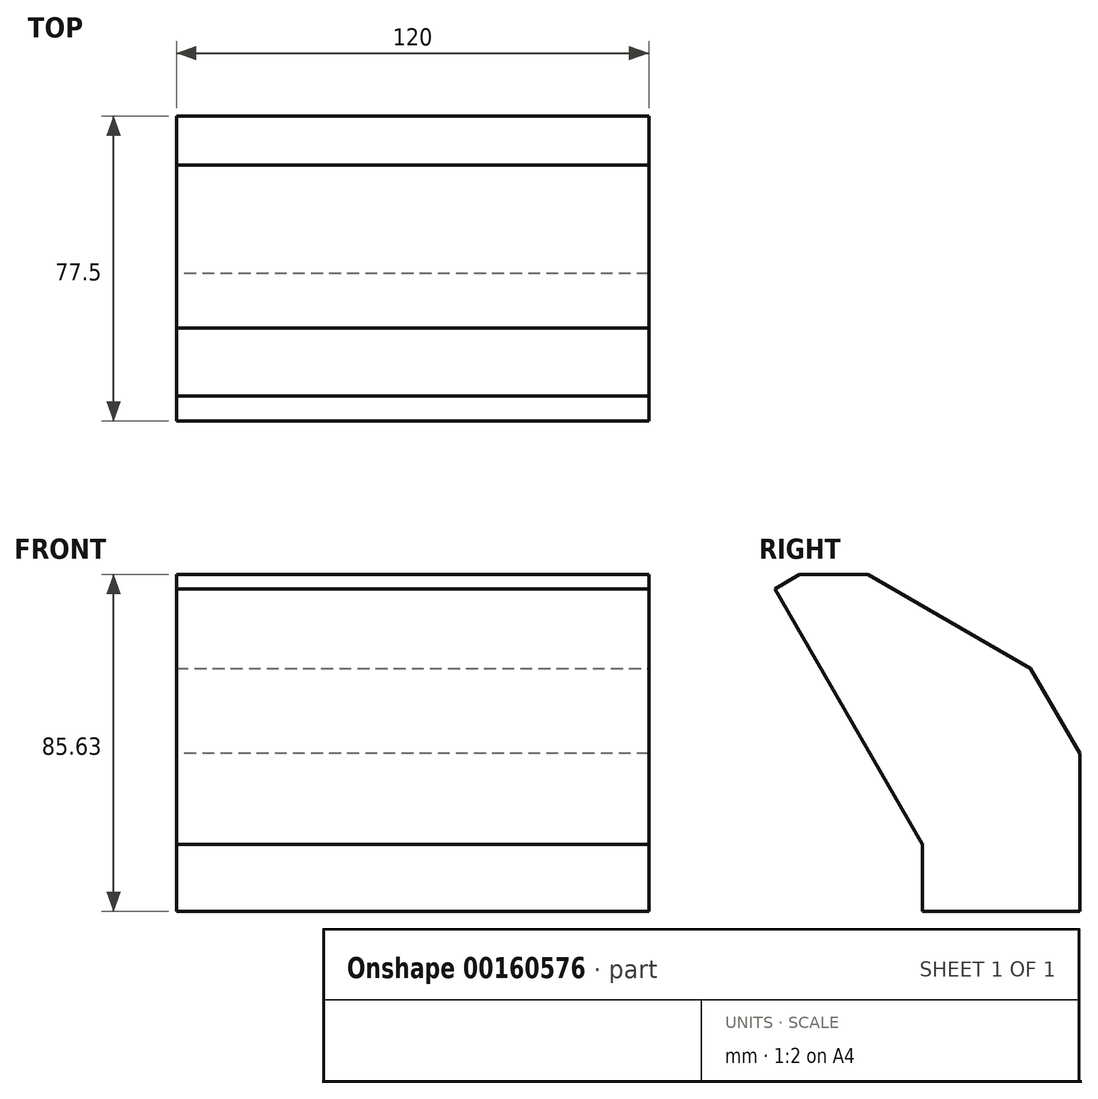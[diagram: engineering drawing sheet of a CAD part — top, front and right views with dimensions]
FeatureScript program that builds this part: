
annotation { "Feature Type Name" : "Feature", "Feature Type Description" : "" }
export const myFeature = defineFeature(function(context is Context, id is Id, definition is map)
    precondition{}
    {
        {
            var Q0;
            Q0=qCreatedBy(makeId("Top.planeOp"),FACE);
            var sketch = newSketch(context, id + "F0", { "sketchPlane" : qUnion([Q0])});
            skLineSegment(sketch, "E0.bottom", {"start": v(60, -20) * mm, "end": v(-60, -20) * mm});
            skLineSegment(sketch, "E0.top", {"start": v(60, 20) * mm, "end": v(-60, 20) * mm});
            skLineSegment(sketch, "E0.left", {"start": v(60, -20) * mm, "end": v(60, 20) * mm});
            skLineSegment(sketch, "E0.right", {"start": v(-60, -20) * mm, "end": v(-60, 20) * mm});
            skPoint(sketch, "E0.middle", {"position": v(0, 0) * mm});
            skLineSegment(sketch, "E1", {"start": v(-60, 0) * mm, "end": v(60, 0) * mm, "construction": true});
            skLineSegment(sketch, "E2", {"start": v(0, 0) * mm, "end": v(-45, 0) * mm, "construction": true});
            skLineSegment(sketch, "E3", {"start": v(0, 0) * mm, "end": v(45, 0) * mm, "construction": true});
            skCircle(sketch, "E4", {"center": v(-45, 0) * mm, "radius": 3 * mm});
            skCircle(sketch, "E5", {"center": v(45, 0) * mm, "radius": 3 * mm});
            skSolve(sketch);
        }
        {
            var Q0;
            Q0=makeQuery(id+"F0.imprint","IMPRINT",FACE,{"disambiguationData":[TD([[makeQuery(id+"F0.imprint","IMPRINT",EDGE,{"derivedFrom":sQuery(id+"F0.wireOp",EDGE,"E0.bottom")}),-1.0]])]});
            var Q1;
            Q1=makeQuery(id+"F0.imprint","IMPRINT",FACE,{"disambiguationData":[TD([[makeQuery(id+"F0.imprint","IMPRINT",EDGE,{"derivedFrom":sQuery(id+"F0.wireOp",EDGE,"E4")}),1.0]])]});
            var Q2;
            Q2=makeQuery(id+"F0.imprint","IMPRINT",FACE,{"disambiguationData":[TD([[makeQuery(id+"F0.imprint","IMPRINT",EDGE,{"derivedFrom":sQuery(id+"F0.wireOp",EDGE,"E5")}),1.0]])]});
            extrude(context, id + "F1", {"entities" : qUnion([Q0, Q1, Q2]), "depth" : 43 * mm});
        }
        {
            var Q0;
            Q0=makeQuery(id+"F1.opExtrude","CAP_EDGE",EDGE,{"disambiguationData":[OSD([sQuery(id+"F0.wireOp",EDGE,"E0.bottom")])],"isStart":false});
            chamfer(context, id + "F2", {"entities" : qUnion([Q0]), "chamferType" : ChamferType.OFFSET_ANGLE, "width" : 45 * mm, "oppositeDirection" : true, "angle" : 30 * degree, "tangentPropagation" : true});
        }
        {
            var Q0;
            Q0=makeQuery(id+"F2.opChamfer","BLEND_FACE",FACE,{"disambiguationData":[OSD([sQuery(id+"F0.wireOp",EDGE,"E0.bottom")])]});
            extrude(context, id + "F3", {"entities" : qUnion([Q0]), "operationType" : NewBodyOperationType.ADD, "depth" : 75 * mm});
        }
        {
            var Q0;
            Q0=makeQuery(id+"F3.opExtrude","CAP_EDGE",EDGE,{"disambiguationData":[OSD([sQuery(id+"F0.wireOp",EDGE,"E0.bottom"),sQuery(id+"F0.wireOp",EDGE,"E0.top")])],"isStart":false});
            chamfer(context, id + "F4", {"entities" : qUnion([Q0]), "chamferType" : ChamferType.OFFSET_ANGLE, "width" : 50 * mm, "oppositeDirection" : false, "angle" : 30 * degree, "tangentPropagation" : true});
        }
        {
            var Q0;
            {var subQ0=sQuery(id+"F0.wireOp",EDGE,"E0.bottom");Q0=makeQuery(id+"F4.opChamfer","BLEND_EDGE",EDGE,{"blendedFrom":[makeQuery(id+"F3.opExtrude","CAP_EDGE",EDGE,{"disambiguationData":[OSD([subQ0,sQuery(id+"F0.wireOp",EDGE,"E0.top")])],"isStart":false}),makeQuery(id+"F3.opExtrude","CAP_FACE",FACE,{"disambiguationData":[OSD([subQ0])],"isStart":false})],"blendedInto":[makeQuery(id+"F3.opExtrude","CAP_FACE",FACE,{"disambiguationData":[OSD([subQ0])],"isStart":false})]});}
            chamfer(context, id + "F5", {"entities" : qUnion([Q0]), "chamferType" : ChamferType.OFFSET_ANGLE, "width" : 10 * mm, "oppositeDirection" : false, "angle" : 30 * degree, "tangentPropagation" : true});
        }
    });
